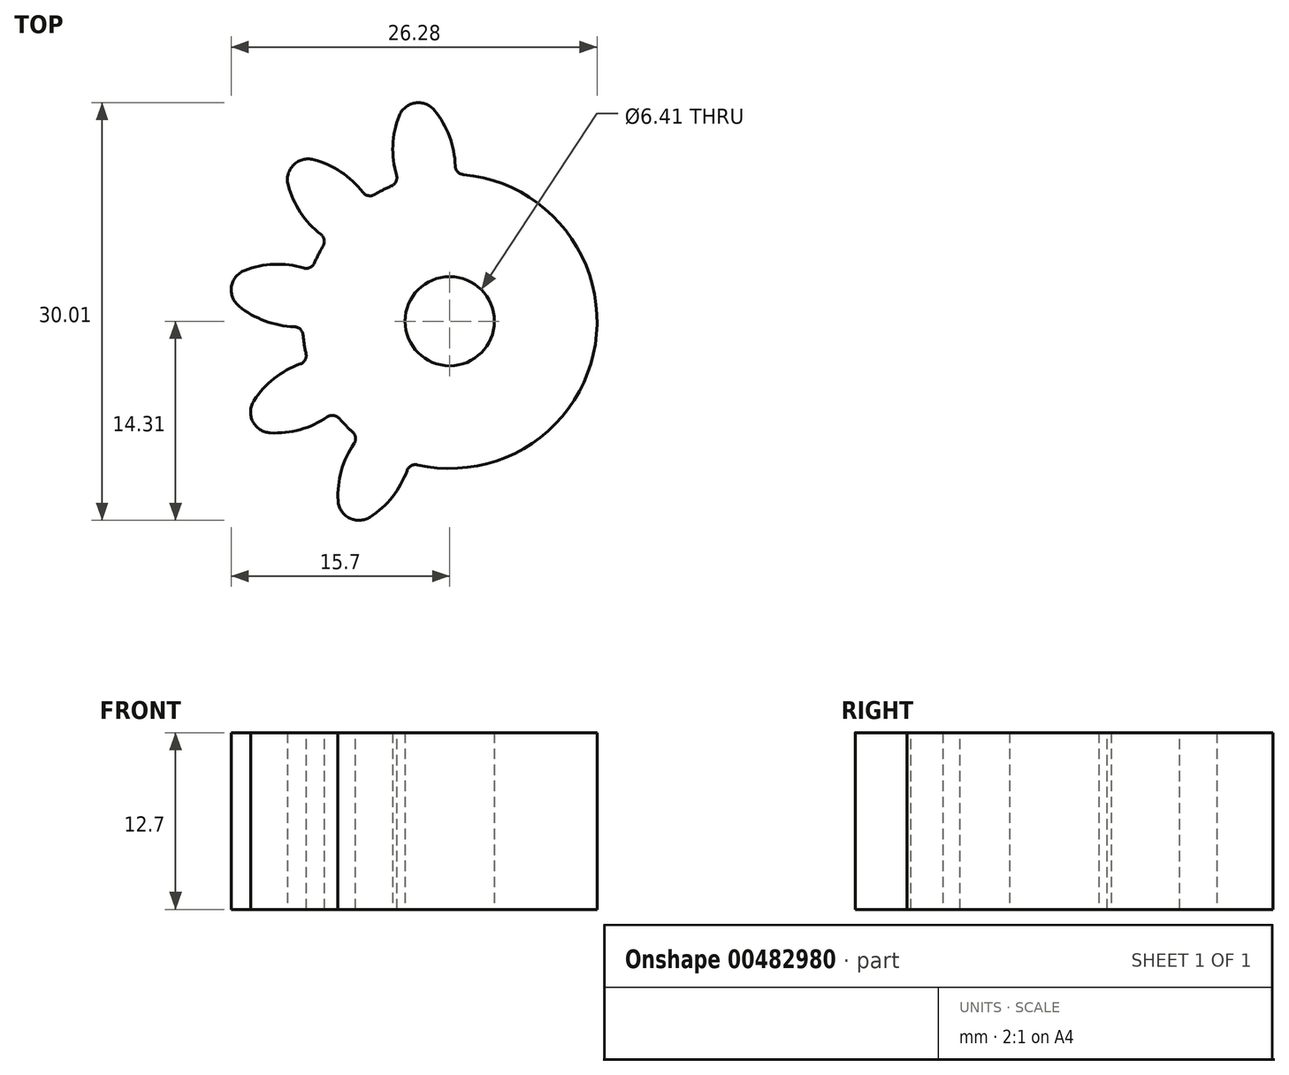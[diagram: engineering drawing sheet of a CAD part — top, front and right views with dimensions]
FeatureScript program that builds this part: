
annotation { "Feature Type Name" : "Feature", "Feature Type Description" : "" }
export const myFeature = defineFeature(function(context is Context, id is Id, definition is map)
    precondition{}
    {
        {
            var Q0;
            Q0=qCreatedBy(makeId("Top.planeOp"),FACE);
            var sketch = newSketch(context, id + "F0", { "sketchPlane" : qUnion([Q0])});
            skCircle(sketch, "E0", {"center": v(0, 0) * mm, "radius": 3.2 * mm});
            skCircle(sketch, "E1", {"center": v(0, 0) * mm, "radius": 10.58 * mm});
            skCircle(sketch, "E2", {"center": v(0, 0) * mm, "radius": 13.23 * mm, "construction": true});
            skCircle(sketch, "E3", {"center": v(0, 0) * mm, "radius": 15.88 * mm, "construction": true});
            skLineSegment(sketch, "E4", {"start": v(0, 0) * mm, "end": v(0, 13.23) * mm, "construction": true});
            skLineSegment(sketch, "E5", {"start": v(0, 13.23) * mm, "end": v(-39.73, 13.23) * mm, "construction": true});
            skLineSegment(sketch, "E6", {"start": v(0, 13.23) * mm, "end": v(-37.9, -0.57) * mm, "construction": true});
            skLineSegment(sketch, "E7", {"start": v(0, 0) * mm, "end": v(-2.48, 15.68) * mm, "construction": true});
            skArc(sketch, "E8", {"start": v(0.39, 10.58) * mm, "mid": v(0.08, 13) * mm, "end": v(-1.09, 15.15) * mm});
            skArc(sketch, "E9.MirrorCS", {"start": v(-3.64, 9.94) * mm, "mid": v(-4.1, 12.34) * mm, "end": v(-3.64, 14.74) * mm});
            skArc(sketch, "E10", {"start": v(-1.09, 15.15) * mm, "mid": v(-2.48, 15.68) * mm, "end": v(-3.64, 14.74) * mm});
            skSolve(sketch);
        }
        {
            var Q0;
            Q0 = qSketchRegion(id + "F0", true);
            extrude(context, id + "F1", {"entities" : qUnion([Q0]), "flatOperationType" : FlatOperationType.REMOVE, "offsetDistance" : 25.4 * mm, "depth" : 12.7 * mm, "domain" : OperationDomain.MODEL});
        }
        {
            var Q0;
            Q0=makeQuery(id+"F1.opExtrude","SWEPT_EDGE",EDGE,{"disambiguationData":[OSD([sQuery(id+"F0.wireOp",EDGE,"E1"),sQuery(id+"F0.wireOp",EDGE,"E9.MirrorCS")])]});
            var Q1;
            Q1=makeQuery(id+"F1.opExtrude","SWEPT_EDGE",EDGE,{"disambiguationData":[OSD([sQuery(id+"F0.wireOp",EDGE,"E1"),sQuery(id+"F0.wireOp",EDGE,"E8")])]});
            fillet(context, id + "F2", {"entities" : qUnion([Q0, Q1]), "radius" : 0.64 * mm, "tangentPropagation" : true, "allowEdgeOverflow" : false});
        }
        {
            var Q0;
            Q0=makeQuery(id+"F2.opFillet","BLEND_FACE",FACE,{"disambiguationData":[OSD([sQuery(id+"F0.wireOp",EDGE,"E1"),sQuery(id+"F0.wireOp",EDGE,"E9.MirrorCS")])]});
            var Q1;
            Q1=makeQuery(id+"F1.opExtrude","SWEPT_FACE",FACE,{"disambiguationData":[OSD([sQuery(id+"F0.wireOp",EDGE,"E9.MirrorCS")])]});
            var Q2;
            Q2=makeQuery(id+"F1.opExtrude","SWEPT_FACE",FACE,{"disambiguationData":[OSD([sQuery(id+"F0.wireOp",EDGE,"E10")])]});
            var Q3;
            Q3=makeQuery(id+"F1.opExtrude","SWEPT_FACE",FACE,{"disambiguationData":[OSD([sQuery(id+"F0.wireOp",EDGE,"E8")])]});
            var Q4;
            Q4=makeQuery(id+"F2.opFillet","BLEND_FACE",FACE,{"disambiguationData":[OSD([sQuery(id+"F0.wireOp",EDGE,"E1"),sQuery(id+"F0.wireOp",EDGE,"E8")])]});
            var Q5;
            Q5=makeQuery(id+"F1.opExtrude","SWEPT_FACE",FACE,{"disambiguationData":[OSD([sQuery(id+"F0.wireOp",EDGE,"E1")])]});
            circularPattern(context, id + "F3", {"patternType" : PatternType.FACE, "faces" : qUnion([Q0, Q1, Q2, Q3, Q4]), "axis" : qUnion([Q5]), "angle" : 144 * degree, "instanceCount" : 5, "oppositeDirection" : true, "equalSpace" : true, "fullFeaturePattern" : false});
        }
    });
